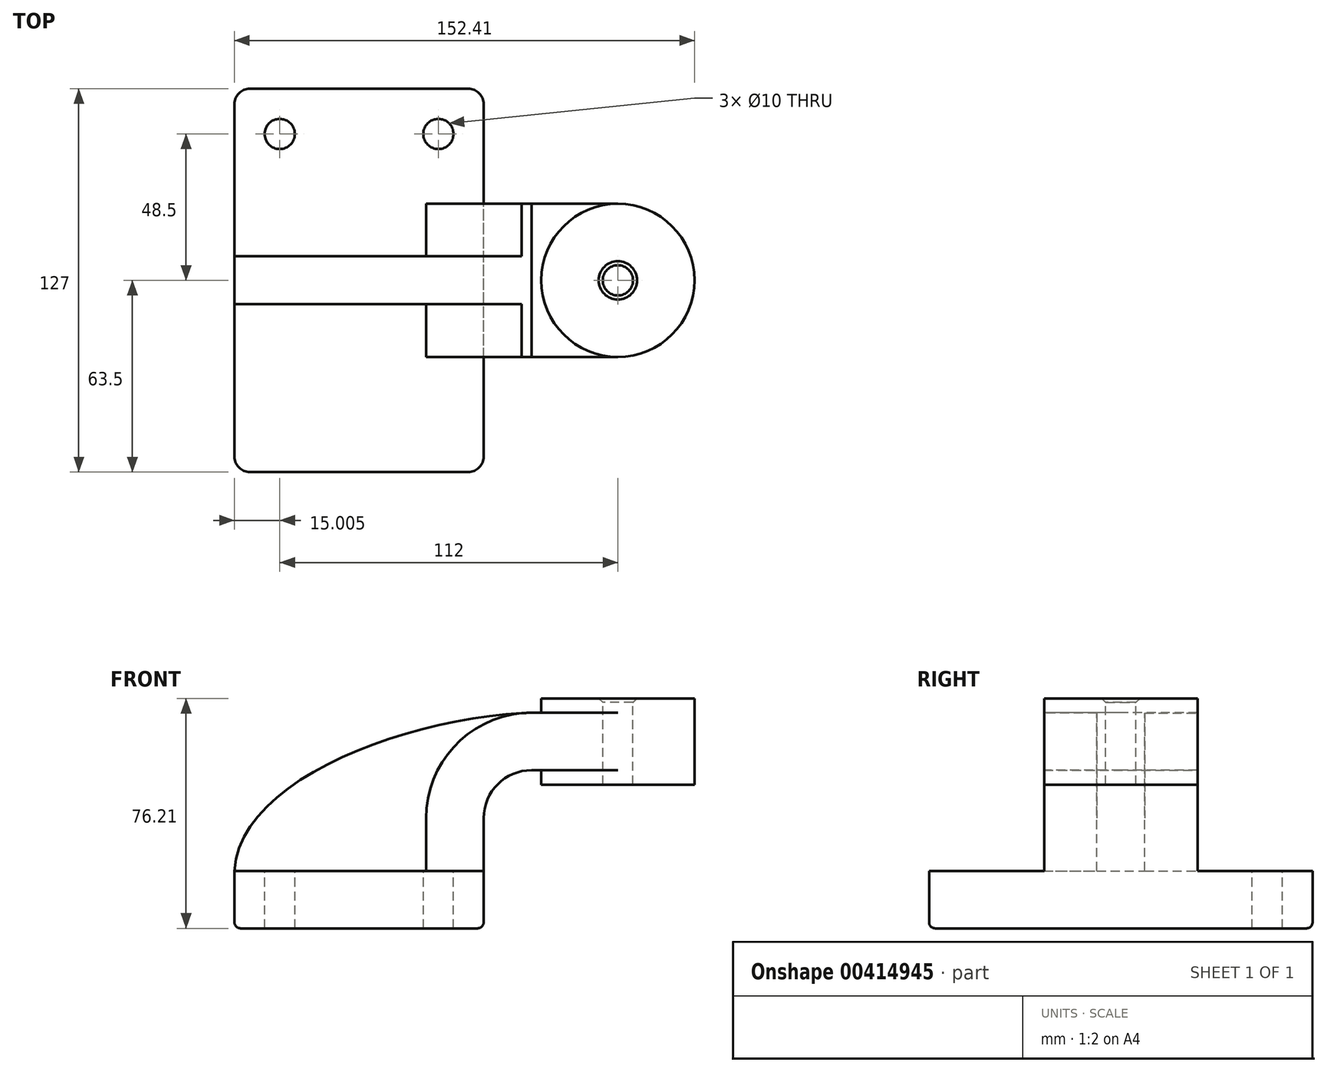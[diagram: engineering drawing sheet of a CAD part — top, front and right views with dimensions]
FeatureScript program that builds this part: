
annotation { "Feature Type Name" : "Feature", "Feature Type Description" : "" }
export const myFeature = defineFeature(function(context is Context, id is Id, definition is map)
    precondition{}
    {
        {
            var Q0;
            Q0=qCreatedBy(makeId("Front.planeOp"),FACE);
            var sketch = newSketch(context, id + "F0", { "sketchPlane" : qUnion([Q0])});
            skLineSegment(sketch, "E0.rect.bottom", {"start": v(-41.28, 9.52) * mm, "end": v(41.28, 9.52) * mm});
            skLineSegment(sketch, "E0.rect.top", {"start": v(-41.28, -9.52) * mm, "end": v(41.28, -9.52) * mm});
            skLineSegment(sketch, "E0.rect.left", {"start": v(-41.28, 9.52) * mm, "end": v(-41.28, -9.52) * mm});
            skLineSegment(sketch, "E0.rect.right", {"start": v(41.28, 9.52) * mm, "end": v(41.28, -9.52) * mm});
            skPoint(sketch, "E0.rect.middle", {"position": v(0, 0) * mm});
            skLineSegment(sketch, "E1", {"start": v(41.28, 9.52) * mm, "end": v(41.28, 27) * mm});
            skArc(sketch, "E2", {"start": v(41.28, 27) * mm, "mid": v(45.92, 38.23) * mm, "end": v(57.15, 42.88) * mm});
            skLineSegment(sketch, "E3", {"start": v(57.15, 42.88) * mm, "end": v(85.72, 42.88) * mm});
            skLineSegment(sketch, "E4.rect.bottom", {"start": v(60.32, 38.1) * mm, "end": v(111.12, 38.1) * mm});
            skLineSegment(sketch, "E4.rect.top", {"start": v(60.32, 66.68) * mm, "end": v(111.12, 66.68) * mm});
            skLineSegment(sketch, "E4.rect.left", {"start": v(60.32, 38.1) * mm, "end": v(60.32, 66.68) * mm});
            skLineSegment(sketch, "E4.rect.right", {"start": v(111.13, 38.1) * mm, "end": v(111.12, 66.68) * mm});
            skPoint(sketch, "E4.rect.middle", {"position": v(85.72, 52.39) * mm});
            skLineSegment(sketch, "E5.0", {"start": v(57.15, 61.93) * mm, "end": v(85.72, 61.93) * mm});
            skArc(sketch, "E5.1", {"start": v(22.23, 27) * mm, "mid": v(32.45, 51.7) * mm, "end": v(57.15, 61.93) * mm});
            skLineSegment(sketch, "E5.2", {"start": v(22.23, 9.52) * mm, "end": v(22.23, 27) * mm});
            skLineSegment(sketch, "E6", {"start": v(85.72, 38.1) * mm, "end": v(85.72, 66.68) * mm});
            skFitSpline(sketch, "E7", {"points": [v(-41.28, 9.53) * mm, v(57.15, 61.93) * mm], "startDerivative": vector(5.2, 92.34) * mm, "endDerivative": vector(120.92, 4.22) * mm});
            skSolve(sketch);
        }
        {
            var Q0;
            Q0=makeQuery(id+"F0.imprint","IMPRINT",FACE,{"disambiguationData":[TD([[makeQuery(id+"F0.imprint","IMPRINT",EDGE,{"derivedFrom":sQuery(id+"F0.wireOp",EDGE,"E0.rect.top")}),1.0]])]});
            extrude(context, id + "F1", {"entities" : qUnion([Q0]), "endBound" : BoundingType.SYMMETRIC, "depth" : 127 * mm});
        }
        {
            var Q0;
            {var subQ9=sQuery(id+"F0.wireOp",EDGE,"E1");Q0=makeQuery(id+"F0.imprint","IMPRINT",FACE,{"disambiguationData":[TD([[makeQuery(id+"F0.imprint","IMPRINT",EDGE,{"derivedFrom":subQ9}),1.0]])]});}
            var Q1;
            {var subQ0=sQuery(id+"F0.wireOp",EDGE,"E6");var subQ1=sQuery(id+"F0.wireOp",EDGE,"E3");var subQ2=makeQuery(id+"F0.imprint","INTERSECT",VERTEX,{"derivedFrom":[subQ1,subQ0]});Q1=makeQuery(id+"F0.imprint","IMPRINT",FACE,{"disambiguationData":[TD([[makeQuery(id+"F0.imprint","IMPRINT",EDGE,{"disambiguationData":[TD([[subQ2,1.0]])],"derivedFrom":subQ1}),1.0]])]});}
            extrude(context, id + "F2", {"entities" : qUnion([Q0, Q1]), "operationType" : NewBodyOperationType.ADD, "endBound" : BoundingType.SYMMETRIC, "depth" : 50.8 * mm});
        }
        {
            var Q0;
            {var subQ3=sQuery(id+"F0.wireOp",EDGE,"E5.2");Q0=makeQuery(id+"F0.imprint","IMPRINT",FACE,{"disambiguationData":[TD([[makeQuery(id+"F0.imprint","IMPRINT",EDGE,{"derivedFrom":subQ3}),1.0]])]});}
            extrude(context, id + "F3", {"entities" : qUnion([Q0]), "operationType" : NewBodyOperationType.ADD, "endBound" : BoundingType.SYMMETRIC, "depth" : 15.88 * mm});
        }
        {
            var Q0;
            {var subQ5=sQuery(id+"F0.wireOp",EDGE,"E4.rect.right");Q0=makeQuery(id+"F0.imprint","IMPRINT",FACE,{"disambiguationData":[TD([[makeQuery(id+"F0.imprint","IMPRINT",EDGE,{"derivedFrom":subQ5}),1.0]])]});}
            var Q1;
            Q1=sQuery(id+"F0.wireOp",EDGE,"E6");
            revolve(context, id + "F4", {"operationType" : NewBodyOperationType.ADD, "entities" : qUnion([Q0]), "axis" : qUnion([Q1]), "revolveType" : RevolveType.FULL});
        }
        {
            var Q0;
            Q0=makeQuery(id+"F1.opExtrude","CAP_EDGE",EDGE,{"disambiguationData":[OSD([sQuery(id+"F0.wireOp",EDGE,"E0.rect.right")])],"isStart":false});
            var Q1;
            Q1=makeQuery(id+"F1.opExtrude","CAP_EDGE",EDGE,{"disambiguationData":[OSD([sQuery(id+"F0.wireOp",EDGE,"E0.rect.left")])],"isStart":false});
            var Q2;
            Q2=makeQuery(id+"F1.opExtrude","CAP_EDGE",EDGE,{"disambiguationData":[OSD([sQuery(id+"F0.wireOp",EDGE,"E0.rect.right")])],"isStart":true});
            var Q3;
            Q3=makeQuery(id+"F1.opExtrude","CAP_EDGE",EDGE,{"disambiguationData":[OSD([sQuery(id+"F0.wireOp",EDGE,"E0.rect.left")])],"isStart":true});
            fillet(context, id + "F5", {"entities" : qUnion([Q0, Q1, Q2, Q3]), "radius" : 5.08 * mm, "tangentPropagation" : true, "allowEdgeOverflow" : false});
        }
        {
            var Q0;
            Q0=makeQuery(id+"F1.opExtrude","CAP_EDGE",EDGE,{"disambiguationData":[OSD([sQuery(id+"F0.wireOp",EDGE,"E0.rect.top")])],"isStart":true});
            fillet(context, id + "F6", {"entities" : qUnion([Q0]), "radius" : 2 * mm, "tangentPropagation" : true, "allowEdgeOverflow" : false});
        }
        {
            var Q0;
            {var subQ4=sQuery(id+"F0.wireOp",EDGE,"E0.rect.bottom");var subQ5=sQuery(id+"F0.wireOp",EDGE,"E0.rect.right");var subQ6=sQuery(id+"F0.wireOp",EDGE,"E0.rect.left");Q0=makeQuery(id+"F3.boolean.opBoolean","SPLIT",FACE,{"disambiguationData":[TD([makeQuery(id+"F1.opExtrude","CAP_FACE",FACE,{"disambiguationData":[OSD([subQ4,sQuery(id+"F0.wireOp",EDGE,"E0.rect.top"),subQ6,subQ5])],"isStart":true})])],"derivedFrom":makeQuery(id+"F1.opExtrude","SWEPT_FACE",FACE,{"disambiguationData":[OSD([subQ4])]})});}
            var sketch = newSketch(context, id + "F7", { "sketchPlane" : qUnion([Q0])});
            skCircle(sketch, "E8", {"center": v(-26.28, 48.5) * mm, "radius": 5 * mm});
            skCircle(sketch, "E9", {"center": v(26.28, 48.5) * mm, "radius": 5 * mm});
            skSolve(sketch);
        }
        {
            var Q0;
            Q0 = qSketchRegion(id + "F7", true);
            extrude(context, id + "F8", {"entities" : qUnion([Q0]), "operationType" : NewBodyOperationType.REMOVE, "endBound" : BoundingType.THROUGH_ALL, "oppositeDirection" : true, "depth" : 25.4 * mm});
        }
        {
            var Q0;
            Q0=makeQuery(id+"F4.opRevolve","SWEPT_FACE",FACE,{"disambiguationData":[OSD([sQuery(id+"F0.wireOp",EDGE,"E4.rect.top")])]});
            var sketch = newSketch(context, id + "F9", { "sketchPlane" : qUnion([Q0])});
            skPoint(sketch, "E10", {"position": v(85.72, 0) * mm});
            skSolve(sketch);
        }
        {
            var Q0;
            Q0=sQuery(id+"F9.wireOp",VERTEX,"E10");
            var Q1;
            Q1=makeQuery(id+"F1.opExtrude","SWEPT_BODY",BODY,{"disambiguationData":[OSD([sQuery(id+"F0.wireOp",EDGE,"E0.rect.bottom"),sQuery(id+"F0.wireOp",EDGE,"E0.rect.top"),sQuery(id+"F0.wireOp",EDGE,"E0.rect.left"),sQuery(id+"F0.wireOp",EDGE,"E0.rect.right")])]});
            hole(context, id + "F10", {"style" : HoleStyle.C_SINK, "endStyle" : HoleEndStyle.THROUGH, "holeDiameter" : 10 * mm, "cSinkDiameter" : 12.7 * mm, "cSinkAngle" : 90 * degree, "isTappedThrough" : true, "tappedDepth" : 12.7 * mm, "tapClearance" : 3, "locations" : qUnion([Q0]), "scope" : qUnion([Q1])});
        }
    });
